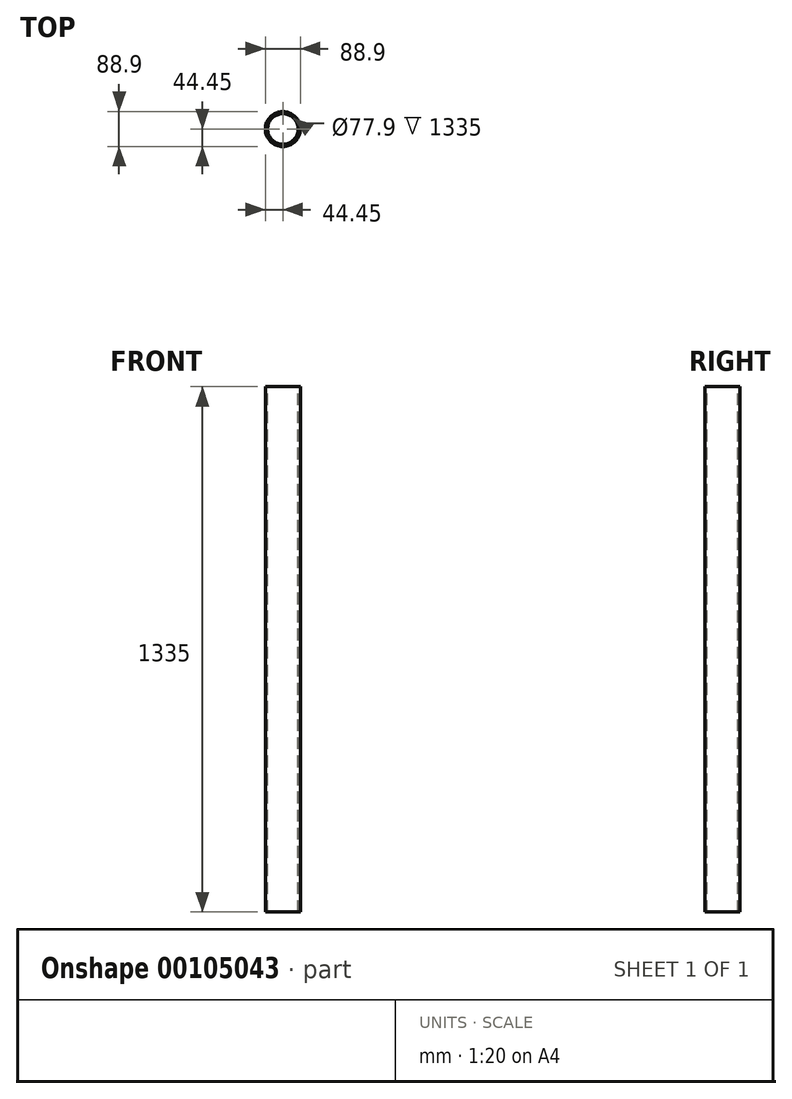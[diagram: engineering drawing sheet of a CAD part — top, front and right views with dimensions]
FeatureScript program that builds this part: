
annotation { "Feature Type Name" : "Feature", "Feature Type Description" : "" }
export const myFeature = defineFeature(function(context is Context, id is Id, definition is map)
    precondition{}
    {
        {
            assignVariable(context, id + "F0", {"name" : "F6", "anyValue" : 1335});
        }
        {
            var Q0;
            Q0=qCreatedBy(makeId("Top.planeOp"),FACE);
            var sketch = newSketch(context, id + "F1", { "sketchPlane" : qUnion([Q0])});
            skCircle(sketch, "E0", {"center": v(0, 0) * mm, "radius": 44.45 * mm});
            skCircle(sketch, "E1", {"center": v(0, 0) * mm, "radius": 38.95 * mm});
            skSolve(sketch);
        }
        {
            var Q0;
            Q0=makeQuery(id+"F1.imprint","IMPRINT",FACE,{"disambiguationData":[TD([[makeQuery(id+"F1.imprint","IMPRINT",EDGE,{"derivedFrom":sQuery(id+"F1.wireOp",EDGE,"E0")}),1.0]])]});
            extrude(context, id + "F2", {"entities" : qUnion([Q0]), "oppositeDirection" : true, "depth" : (getVariable(context, 'F6')) * mm});
        }
    });
